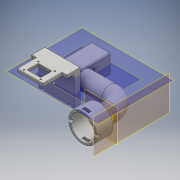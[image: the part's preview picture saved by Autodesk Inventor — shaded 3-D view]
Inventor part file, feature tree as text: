
AUTODESK INVENTOR PART (.ipt)
format: ipt  version: 2016 (Build 200138000, 138)  size: 544,768 bytes
history: native  units: mm
features: sketch x25, extrude x21, fillet x11, other x8, loft x2, projected_geometry x2, sweep x1
ambient origin geometry x8: Origin, YZ Plane, XZ Plane, XY Plane, X Axis, Y Axis, Z Axis, Center Point
bodies: Body1 (feature_tree)
feature tree (70):
  other  "ソリッド1"
  extrude  "押し出し1"  Depth=13.0mm TaperAngle=0.0deg
  fillet  "フィレット1"  Radius=1.0mm
  fillet  "フィレット2"  Radius=10.0mm
  sketch  "スケッチ2"
  extrude  "押し出し2"  Depth=10.0mm
  extrude  "押し出し3"  Depth=4.0mm TaperAngle=0.0deg
  sketch  "スケッチ3"
  extrude  "押し出し4"  Depth=4.0mm TaperAngle=0.0deg
  extrude  "押し出し5"  Depth=13.0mm
  extrude  "押し出し6"  Depth=13.0mm
  extrude  "押し出し7"  Depth=7.0mm TaperAngle=0.0deg
  fillet  "フィレット3"  Radius=7.0mm
  extrude  "押し出し8"  Depth=40.0mm
  extrude  "押し出し9"  Depth=40.0mm
  sketch  "スケッチ9"
  other  "作業平面1"
  sweep  "スイープ1"
  extrude  "押し出し10"  Depth=17.5mm
  sketch  "スケッチ12"
  other  "作業平面2"
  loft  "ロフト1"
  other  "作業平面3"
  loft  "ロフト2"
  extrude  "押し出し11"  Depth=25.0mm
  extrude  "押し出し12"  Depth=55.0mm TaperAngle=0.0deg
  fillet  "フィレット4"  Radius=20.0mm
  fillet  "フィレット5"  Radius=2.0mm
  other  "作業平面4"
  extrude  "押し出し13"  Depth=4.0mm
  other  "作業平面5"
  extrude  "押し出し14"  Depth=4.0mm
  extrude  "押し出し15"  Depth=4.0mm
  fillet  "フィレット6"  Radius=4.0mm
  fillet  "フィレット7"  Radius=2.0mm
  extrude  "押し出し20"  Depth=90.0mm TaperAngle=0.0deg
  extrude  "押し出し21"  Depth=4.0mm
  fillet  "フィレット8"  Radius=73.0mm
  fillet  "フィレット9"  Radius=14.0mm
  extrude  "押し出し25"  TaperAngle=90.0deg  [1 undecoded]
  extrude  "押し出し26"  TaperAngle=0.0deg  [1 undecoded]
  extrude  "押し出し27"  Depth=12.0mm TaperAngle=0.0deg
  extrude  "押し出し28"  Depth=12.0mm
  fillet  "フィレット10"  Radius=60.0mm
  fillet  "フィレット11"  [1 undecoded]
  sketch  "スケッチ1"
  sketch  "スケッチ4"
  sketch  "スケッチ5"
  sketch  "スケッチ6"
  sketch  "スケッチ7"
  sketch  "スケッチ10"
  sketch  "スケッチ11"
  projected_geometry  "投影ループ1"
  sketch  "スケッチ13"
  other  "エッジ1"
  sketch  "スケッチ15"
  sketch  "スケッチ18"
  sketch  "スケッチ19"
  sketch  "スケッチ20"
  projected_geometry  "投影ループ2"
  sketch  "スケッチ21"
  sketch  "スケッチ22"
  sketch  "スケッチ23"
  sketch  "スケッチ27"
  sketch  "スケッチ28"
  sketch  "スケッチ32"
  sketch  "スケッチ33"
  sketch  "スケッチ34"
  sketch  "スケッチ35"
  other  "断面エッジを投影1"
note: 3 required parameter values undecoded (feature->parameter linkage not recoverable at this tier; creation-order binding heuristic only, values carry confidence <= 0.55)
